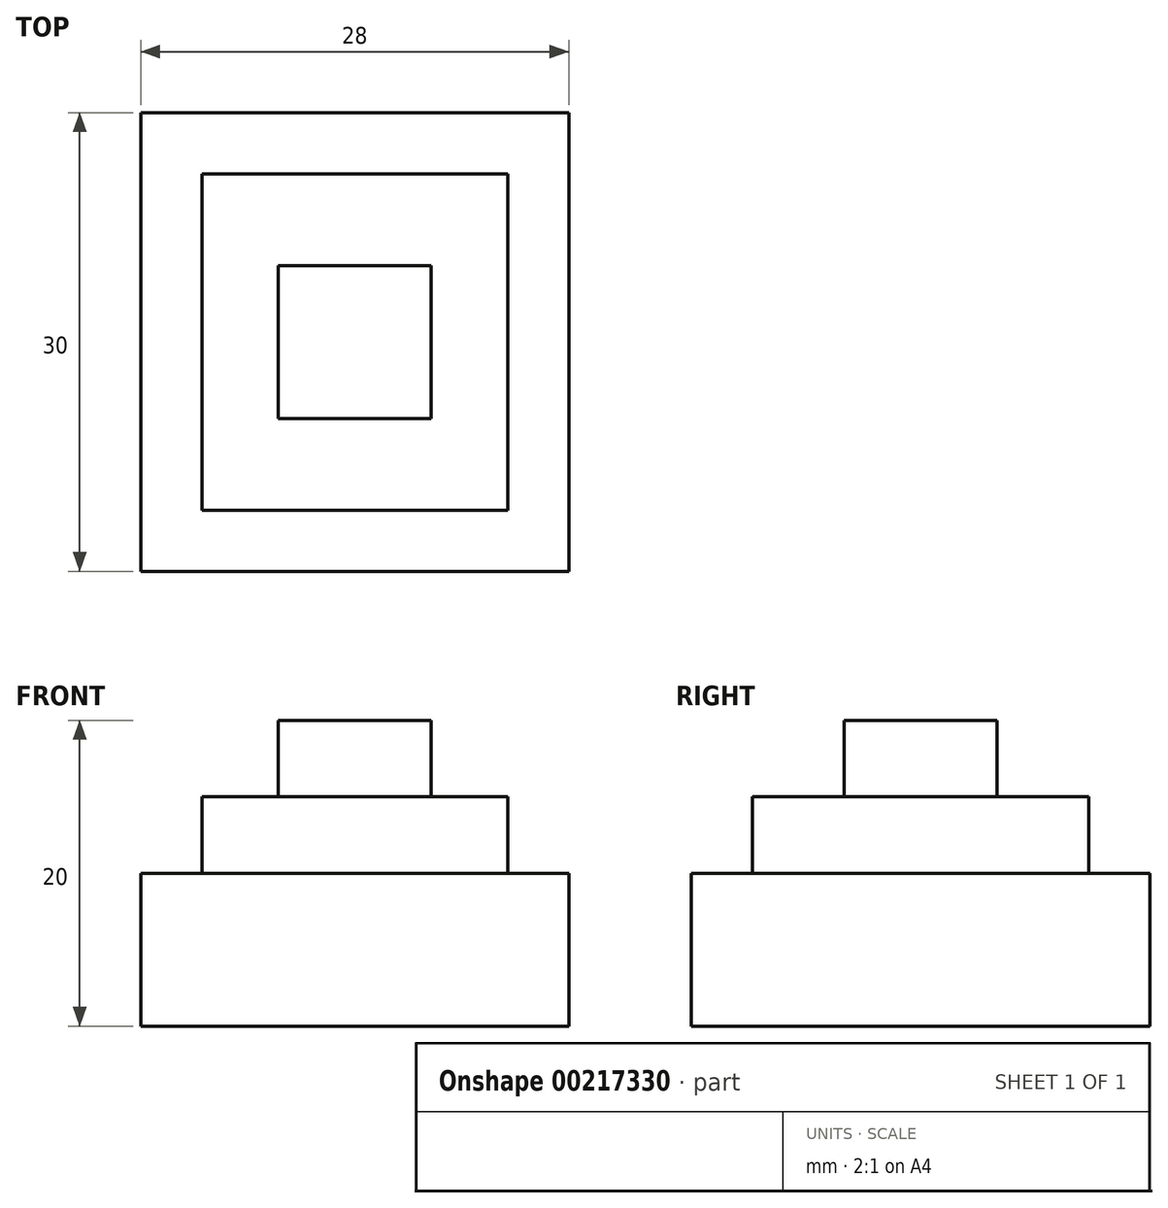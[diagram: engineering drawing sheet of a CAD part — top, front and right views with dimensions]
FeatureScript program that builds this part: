
annotation { "Feature Type Name" : "Feature", "Feature Type Description" : "" }
export const myFeature = defineFeature(function(context is Context, id is Id, definition is map)
    precondition{}
    {
        {
            var Q0;
            Q0=qCreatedBy(makeId("Top.planeOp"),FACE);
            var sketch = newSketch(context, id + "F0", { "sketchPlane" : qUnion([Q0])});
            skLineSegment(sketch, "E0.bottom", {"start": v(14, 15) * mm, "end": v(-14, 15) * mm});
            skLineSegment(sketch, "E0.top", {"start": v(14, -15) * mm, "end": v(-14, -15) * mm});
            skLineSegment(sketch, "E0.left", {"start": v(14, 15) * mm, "end": v(14, -15) * mm});
            skLineSegment(sketch, "E0.right", {"start": v(-14, 15) * mm, "end": v(-14, -15) * mm});
            skPoint(sketch, "E0.middle", {"position": v(0, 0) * mm});
            skLineSegment(sketch, "E1.bottom", {"start": v(10, 11) * mm, "end": v(-10, 11) * mm});
            skLineSegment(sketch, "E1.top", {"start": v(10, -11) * mm, "end": v(-10, -11) * mm});
            skLineSegment(sketch, "E1.left", {"start": v(10, 11) * mm, "end": v(10, -11) * mm});
            skLineSegment(sketch, "E1.right", {"start": v(-10, 11) * mm, "end": v(-10, -11) * mm});
            skSolve(sketch);
        }
        {
            var Q0;
            Q0 = qSketchRegion(id + "F0", true);
            extrude(context, id + "F1", {"entities" : qUnion([Q0]), "depth" : 10 * mm});
        }
        {
            var Q0;
            Q0=makeQuery(id+"F0.imprint","IMPRINT",FACE,{"disambiguationData":[TD([[makeQuery(id+"F0.imprint","IMPRINT",EDGE,{"derivedFrom":sQuery(id+"F0.wireOp",EDGE,"E1.bottom")}),1.0]])]});
            extrude(context, id + "F2", {"entities" : qUnion([Q0]), "operationType" : NewBodyOperationType.ADD, "depth" : 15 * mm});
        }
        {
            var Q0;
            Q0=makeQuery(id+"F2.opExtrude","CAP_FACE",FACE,{"disambiguationData":[OSD([sQuery(id+"F0.wireOp",EDGE,"E1.bottom"),sQuery(id+"F0.wireOp",EDGE,"E1.top"),sQuery(id+"F0.wireOp",EDGE,"E1.left"),sQuery(id+"F0.wireOp",EDGE,"E1.right")])],"isStart":false});
            var sketch = newSketch(context, id + "F3", { "sketchPlane" : qUnion([Q0])});
            skLineSegment(sketch, "E2.bottom", {"start": v(5, 5) * mm, "end": v(-5, 5) * mm});
            skLineSegment(sketch, "E2.top", {"start": v(5, -5) * mm, "end": v(-5, -5) * mm});
            skLineSegment(sketch, "E2.left", {"start": v(5, 5) * mm, "end": v(5, -5) * mm});
            skLineSegment(sketch, "E2.right", {"start": v(-5, 5) * mm, "end": v(-5, -5) * mm});
            skPoint(sketch, "E2.middle", {"position": v(0, 0) * mm});
            skSolve(sketch);
        }
        {
            var Q0;
            Q0=makeQuery(id+"F3.imprint","IMPRINT",FACE,{"disambiguationData":[TD([[makeQuery(id+"F3.imprint","IMPRINT",EDGE,{"derivedFrom":sQuery(id+"F3.wireOp",EDGE,"E2.bottom")}),1.0]])]});
            extrude(context, id + "F4", {"entities" : qUnion([Q0]), "operationType" : NewBodyOperationType.ADD, "depth" : 5 * mm});
        }
    });
